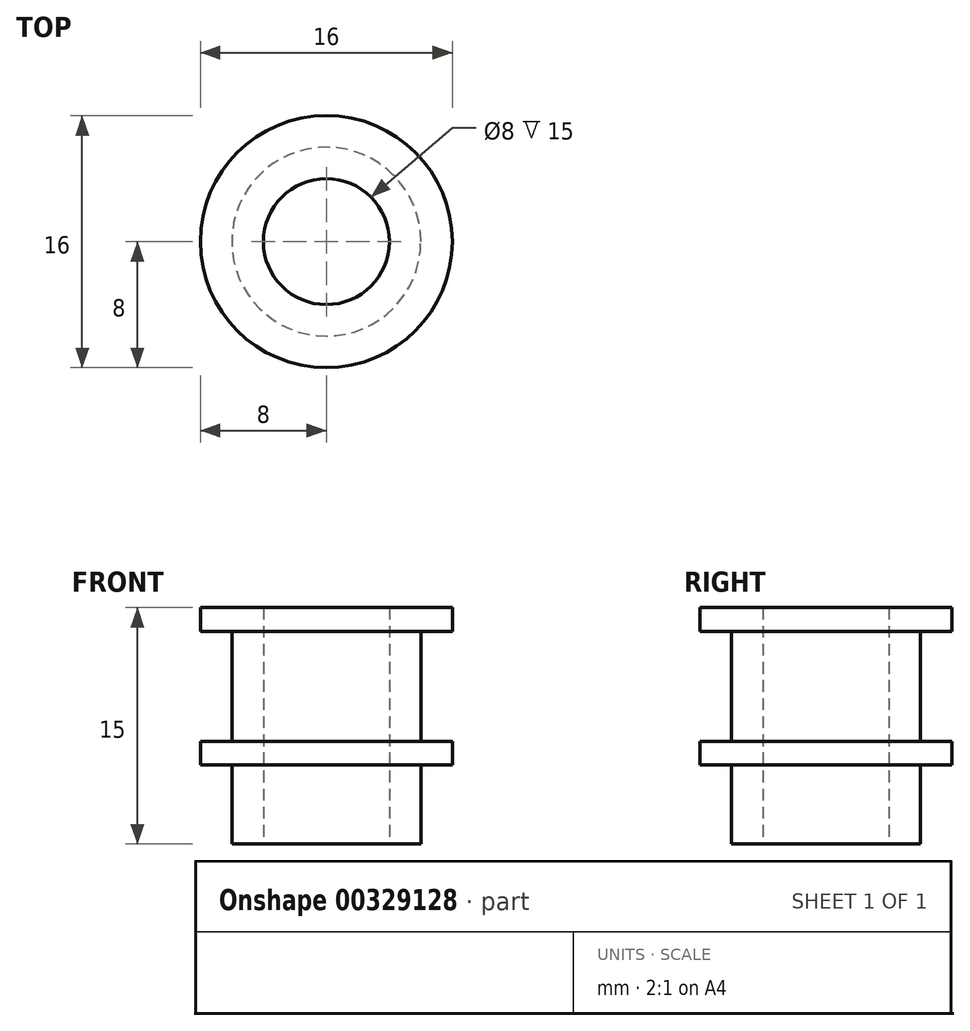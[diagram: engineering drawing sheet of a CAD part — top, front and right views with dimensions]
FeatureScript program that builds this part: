
annotation { "Feature Type Name" : "Feature", "Feature Type Description" : "" }
export const myFeature = defineFeature(function(context is Context, id is Id, definition is map)
    precondition{}
    {
        {
            var Q0;
            Q0=qCreatedBy(makeId("Front.planeOp"),FACE);
            var sketch = newSketch(context, id + "F0", { "sketchPlane" : qUnion([Q0])});
            skLineSegment(sketch, "E0", {"start": v(0, 0) * mm, "end": v(0, 15) * mm, "construction": true});
            skLineSegment(sketch, "E1", {"start": v(4, 0) * mm, "end": v(4, 15) * mm});
            skLineSegment(sketch, "E2", {"start": v(4, 15) * mm, "end": v(8, 15) * mm});
            skLineSegment(sketch, "E3", {"start": v(8, 15) * mm, "end": v(8, 13.5) * mm});
            skLineSegment(sketch, "E4", {"start": v(8, 13.5) * mm, "end": v(6, 13.5) * mm});
            skLineSegment(sketch, "E5", {"start": v(6, 13.5) * mm, "end": v(6, 6.5) * mm});
            skLineSegment(sketch, "E6", {"start": v(6, 6.5) * mm, "end": v(8, 6.5) * mm});
            skLineSegment(sketch, "E7", {"start": v(8, 6.5) * mm, "end": v(8, 5) * mm});
            skLineSegment(sketch, "E8", {"start": v(8, 5) * mm, "end": v(6, 5) * mm});
            skLineSegment(sketch, "E9", {"start": v(6, 5) * mm, "end": v(6, 0) * mm});
            skLineSegment(sketch, "E10", {"start": v(6, 0) * mm, "end": v(4, 0) * mm});
            skSolve(sketch);
        }
        {
            var Q0;
            Q0=qSketchRegion(id+"F0",true);
            var Q1;
            Q1=sQuery(id+"F0.wireOp",EDGE,"E0");
            revolve(context, id + "F1", {"entities" : qUnion([Q0]), "axis" : qUnion([Q1]), "revolveType" : RevolveType.FULL});
        }
    });
